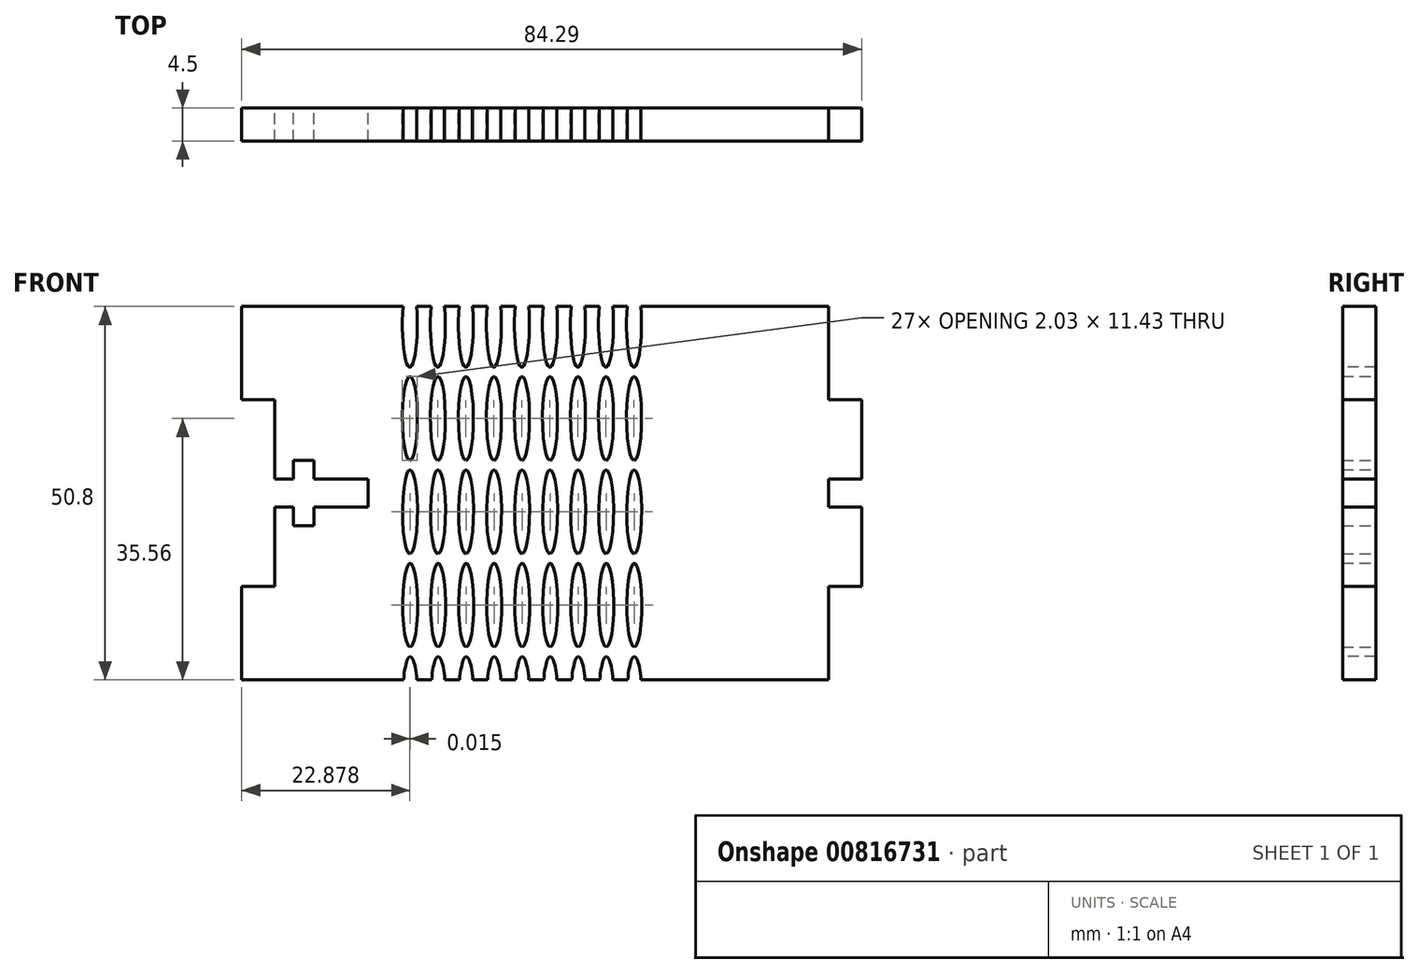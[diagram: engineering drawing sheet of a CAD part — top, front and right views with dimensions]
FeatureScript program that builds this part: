
annotation { "Feature Type Name" : "Feature", "Feature Type Description" : "" }
export const myFeature = defineFeature(function(context is Context, id is Id, definition is map)
    precondition{}
    {
        {
            var Q0;
            Q0=qCreatedBy(makeId("Front.planeOp"),FACE);
            var sketch = newSketch(context, id + "F0", { "sketchPlane" : qUnion([Q0])});
            skLineSegment(sketch, "E0.bottom", {"start": v(39.9, -25.4) * mm, "end": v(14.41, -25.4) * mm});
            skLineSegment(sketch, "E0.top", {"start": v(39.9, 25.4) * mm, "end": v(14.35, 25.4) * mm});
            skLineSegment(sketch, "E0.left", {"start": v(39.9, -25.4) * mm, "end": v(39.9, -12.7) * mm});
            skLineSegment(sketch, "E0.right", {"start": v(-39.9, -25.4) * mm, "end": v(-39.9, -12.7) * mm});
            skPoint(sketch, "E0.middle", {"position": v(0, 0) * mm});
            skLineSegment(sketch, "E1.bottom", {"start": v(-35.4, -12.7) * mm, "end": v(-39.9, -12.7) * mm});
            skLineSegment(sketch, "E1.top", {"start": v(-35.4, 12.7) * mm, "end": v(-39.9, 12.7) * mm});
            skLineSegment(sketch, "E1.left", {"start": v(-35.4, -12.7) * mm, "end": v(-35.4, -1.9) * mm});
            skPoint(sketch, "E1.middle", {"position": v(-39.9, 0) * mm});
            skLineSegment(sketch, "E2.bottom", {"start": v(-35.4, 1.9) * mm, "end": v(-32.86, 1.9) * mm});
            skLineSegment(sketch, "E2.top", {"start": v(-35.4, -1.9) * mm, "end": v(-32.86, -1.9) * mm});
            skLineSegment(sketch, "E2.right", {"start": v(-22.7, 1.9) * mm, "end": v(-22.7, -1.9) * mm});
            skPoint(sketch, "E2.middle", {"position": v(-29.05, 0) * mm});
            skPoint(sketch, "E2.middle.positionSnap0", {"position": v(-35.4, 0) * mm});
            skPoint(sketch, "E2.centerSnap0", {"position": v(-35.4, 0) * mm});
            skLineSegment(sketch, "E3.bottom", {"start": v(-30.07, -4.45) * mm, "end": v(-32.86, -4.45) * mm});
            skLineSegment(sketch, "E3.top", {"start": v(-30.07, 4.45) * mm, "end": v(-32.86, 4.45) * mm});
            skLineSegment(sketch, "E3.left", {"start": v(-30.07, -4.45) * mm, "end": v(-30.07, -1.9) * mm});
            skLineSegment(sketch, "E3.right", {"start": v(-32.86, -4.45) * mm, "end": v(-32.86, -1.9) * mm});
            skPoint(sketch, "E3.middle", {"position": v(-31.46, 0) * mm});
            skPoint(sketch, "E1.right.end.orphan", {"position": v(-44.4, 12.7) * mm});
            skPoint(sketch, "E4.orphan", {"position": v(-44.4, -12.7) * mm});
            skLineSegment(sketch, "E5.trimOffspring", {"start": v(-30.07, 1.9) * mm, "end": v(-22.7, 1.9) * mm});
            skLineSegment(sketch, "E6.trimOffspring", {"start": v(-30.07, -1.9) * mm, "end": v(-22.7, -1.9) * mm});
            skLineSegment(sketch, "E7.trimOffspring", {"start": v(-32.86, 1.9) * mm, "end": v(-32.86, 4.45) * mm});
            skLineSegment(sketch, "E8.trimOffspring", {"start": v(-30.07, 1.9) * mm, "end": v(-30.07, 4.45) * mm});
            skLineSegment(sketch, "E9.trimOffspring", {"start": v(-35.4, 1.9) * mm, "end": v(-35.4, 12.7) * mm});
            skLineSegment(sketch, "E10.trimOffspring", {"start": v(-39.9, 12.7) * mm, "end": v(-39.9, 25.4) * mm});
            skLineSegment(sketch, "E11.trimOffspring", {"start": v(39.9, 12.7) * mm, "end": v(39.9, 25.4) * mm});
            skLineSegment(sketch, "E12.bottom", {"start": v(39.9, 12.7) * mm, "end": v(44.4, 12.7) * mm});
            skLineSegment(sketch, "E12.top", {"start": v(39.69, -12.7) * mm, "end": v(44.4, -12.7) * mm});
            skLineSegment(sketch, "E12.right", {"start": v(44.4, 12.7) * mm, "end": v(44.4, 1.9) * mm});
            skPoint(sketch, "E13.MirrorCS.start.orphan", {"position": v(35.4, 12.7) * mm});
            skPoint(sketch, "E14.MirrorCS.start.orphan", {"position": v(35.4, -12.7) * mm});
            skLineSegment(sketch, "E15.bottom", {"start": v(44.4, -1.9) * mm, "end": v(39.9, -1.9) * mm});
            skLineSegment(sketch, "E15.top", {"start": v(44.4, 1.9) * mm, "end": v(39.9, 1.9) * mm});
            skLineSegment(sketch, "E15.right", {"start": v(39.9, -1.9) * mm, "end": v(39.9, 1.9) * mm});
            skPoint(sketch, "E15.middle", {"position": v(42.14, 0) * mm});
            skLineSegment(sketch, "E16.trimOffspring", {"start": v(44.4, -1.9) * mm, "end": v(44.4, -12.7) * mm});
            skEllipticalArc(sketch, "E17", {});
            skEllipse(sketch, "E18.0.1.0", {"center": v(-17.02, 10.16) * mm, "majorRadius": 5.72 * mm, "minorRadius": 1.02 * mm, "majorAxis": v(0, -1)});
            skEllipse(sketch, "E18.0.2.0", {"center": v(-17, -2.54) * mm, "majorRadius": 5.72 * mm, "minorRadius": 1.02 * mm, "majorAxis": v(0, -1)});
            skEllipse(sketch, "E18.0.3.0", {"center": v(-17, -15.24) * mm, "majorRadius": 5.72 * mm, "minorRadius": 1.02 * mm, "majorAxis": v(0, -1)});
            skEllipticalArc(sketch, "E18.0.4.0", {});
            skEllipticalArc(sketch, "E18.1.0.0", {});
            skEllipse(sketch, "E18.1.1.0", {"center": v(-13.21, 10.16) * mm, "majorRadius": 5.72 * mm, "minorRadius": 1.02 * mm, "majorAxis": v(0, -1)});
            skEllipse(sketch, "E18.1.2.0", {"center": v(-13.2, -2.54) * mm, "majorRadius": 5.72 * mm, "minorRadius": 1.02 * mm, "majorAxis": v(0, -1)});
            skEllipse(sketch, "E18.1.3.0", {"center": v(-13.18, -15.24) * mm, "majorRadius": 5.72 * mm, "minorRadius": 1.02 * mm, "majorAxis": v(0, -1)});
            skEllipticalArc(sketch, "E18.1.4.0", {});
            skEllipticalArc(sketch, "E18.2.0.0", {});
            skEllipse(sketch, "E18.2.1.0", {"center": v(-9.4, 10.16) * mm, "majorRadius": 5.72 * mm, "minorRadius": 1.02 * mm, "majorAxis": v(0, -1)});
            skEllipse(sketch, "E18.2.2.0", {"center": v(-9.39, -2.54) * mm, "majorRadius": 5.72 * mm, "minorRadius": 1.02 * mm, "majorAxis": v(0, -1)});
            skEllipse(sketch, "E18.2.3.0", {"center": v(-9.37, -15.24) * mm, "majorRadius": 5.72 * mm, "minorRadius": 1.02 * mm, "majorAxis": v(0, -1)});
            skEllipticalArc(sketch, "E18.2.4.0", {});
            skEllipticalArc(sketch, "E18.3.0.0", {});
            skEllipse(sketch, "E18.3.1.0", {"center": v(-5.6, 10.16) * mm, "majorRadius": 5.72 * mm, "minorRadius": 1.02 * mm, "majorAxis": v(0, -1)});
            skEllipse(sketch, "E18.3.2.0", {"center": v(-5.58, -2.54) * mm, "majorRadius": 5.72 * mm, "minorRadius": 1.02 * mm, "majorAxis": v(0, -1)});
            skEllipse(sketch, "E18.3.3.0", {"center": v(-5.56, -15.24) * mm, "majorRadius": 5.72 * mm, "minorRadius": 1.02 * mm, "majorAxis": v(0, -1)});
            skEllipticalArc(sketch, "E18.3.4.0", {});
            skEllipticalArc(sketch, "E18.4.0.0", {});
            skEllipse(sketch, "E18.4.1.0", {"center": v(-1.78, 10.16) * mm, "majorRadius": 5.72 * mm, "minorRadius": 1.02 * mm, "majorAxis": v(0, -1)});
            skEllipse(sketch, "E18.4.2.0", {"center": v(-1.77, -2.54) * mm, "majorRadius": 5.72 * mm, "minorRadius": 1.02 * mm, "majorAxis": v(0, -1)});
            skEllipse(sketch, "E18.4.3.0", {"center": v(-1.75, -15.24) * mm, "majorRadius": 5.72 * mm, "minorRadius": 1.02 * mm, "majorAxis": v(0, -1)});
            skEllipticalArc(sketch, "E18.4.4.0", {});
            skEllipticalArc(sketch, "E18.5.0.0", {});
            skEllipse(sketch, "E18.5.1.0", {"center": v(2.03, 10.16) * mm, "majorRadius": 5.72 * mm, "minorRadius": 1.02 * mm, "majorAxis": v(0, -1)});
            skEllipse(sketch, "E18.5.2.0", {"center": v(2.04, -2.54) * mm, "majorRadius": 5.72 * mm, "minorRadius": 1.02 * mm, "majorAxis": v(0, -1)});
            skEllipse(sketch, "E18.5.3.0", {"center": v(2.06, -15.24) * mm, "majorRadius": 5.72 * mm, "minorRadius": 1.02 * mm, "majorAxis": v(0, -1)});
            skEllipticalArc(sketch, "E18.5.4.0", {});
            skEllipticalArc(sketch, "E18.6.0.0", {});
            skEllipse(sketch, "E18.6.1.0", {"center": v(5.84, 10.16) * mm, "majorRadius": 5.72 * mm, "minorRadius": 1.02 * mm, "majorAxis": v(0, -1)});
            skEllipse(sketch, "E18.6.2.0", {"center": v(5.85, -2.54) * mm, "majorRadius": 5.72 * mm, "minorRadius": 1.02 * mm, "majorAxis": v(0, -1)});
            skEllipse(sketch, "E18.6.3.0", {"center": v(5.87, -15.24) * mm, "majorRadius": 5.72 * mm, "minorRadius": 1.02 * mm, "majorAxis": v(0, -1)});
            skEllipticalArc(sketch, "E18.6.4.0", {});
            skEllipticalArc(sketch, "E18.7.0.0", {});
            skEllipse(sketch, "E18.7.1.0", {"center": v(9.65, 10.16) * mm, "majorRadius": 5.72 * mm, "minorRadius": 1.02 * mm, "majorAxis": v(0, -1)});
            skEllipse(sketch, "E18.7.2.0", {"center": v(9.66, -2.54) * mm, "majorRadius": 5.72 * mm, "minorRadius": 1.02 * mm, "majorAxis": v(0, -1)});
            skEllipse(sketch, "E18.7.3.0", {"center": v(9.68, -15.24) * mm, "majorRadius": 5.72 * mm, "minorRadius": 1.02 * mm, "majorAxis": v(0, -1)});
            skEllipticalArc(sketch, "E18.7.4.0", {});
            skEllipticalArc(sketch, "E18.8.0.0", {});
            skEllipse(sketch, "E18.8.1.0", {"center": v(13.46, 10.16) * mm, "majorRadius": 5.72 * mm, "minorRadius": 1.02 * mm, "majorAxis": v(0, -1)});
            skEllipse(sketch, "E18.8.2.0", {"center": v(13.47, -2.54) * mm, "majorRadius": 5.72 * mm, "minorRadius": 1.02 * mm, "majorAxis": v(0, -1)});
            skEllipse(sketch, "E18.8.3.0", {"center": v(13.49, -15.24) * mm, "majorRadius": 5.72 * mm, "minorRadius": 1.02 * mm, "majorAxis": v(0, -1)});
            skEllipticalArc(sketch, "E18.8.4.0", {});
            skLineSegment(sketch, "E18.direction1", {"start": v(-17.04, 22.86) * mm, "end": v(-13.23, 22.86) * mm, "construction": true});
            skLineSegment(sketch, "E18.direction2", {"start": v(-17.04, 22.86) * mm, "end": v(-17.02, 10.16) * mm, "construction": true});
            skLineSegment(sketch, "E19.trimOffspring", {"start": v(-17.89, -25.4) * mm, "end": v(-39.9, -25.4) * mm});
            skLineSegment(sketch, "E20.trimOffspring", {"start": v(-14.08, -25.4) * mm, "end": v(-16.07, -25.4) * mm});
            skLineSegment(sketch, "E21.trimOffspring", {"start": v(-10.27, -25.4) * mm, "end": v(-12.26, -25.4) * mm});
            skLineSegment(sketch, "E22.trimOffspring", {"start": v(-6.46, -25.4) * mm, "end": v(-8.45, -25.4) * mm});
            skLineSegment(sketch, "E23.trimOffspring", {"start": v(-2.65, -25.4) * mm, "end": v(-4.64, -25.4) * mm});
            skLineSegment(sketch, "E24.trimOffspring", {"start": v(1.16, -25.4) * mm, "end": v(-0.83, -25.4) * mm});
            skLineSegment(sketch, "E25.trimOffspring", {"start": v(4.97, -25.4) * mm, "end": v(2.98, -25.4) * mm});
            skLineSegment(sketch, "E26.trimOffspring", {"start": v(8.78, -25.4) * mm, "end": v(6.8, -25.4) * mm});
            skLineSegment(sketch, "E27.trimOffspring", {"start": v(12.6, -25.4) * mm, "end": v(10.6, -25.4) * mm});
            skLineSegment(sketch, "E28.trimOffspring", {"start": v(12.53, 25.4) * mm, "end": v(10.54, 25.4) * mm});
            skLineSegment(sketch, "E29.trimOffspring", {"start": v(8.72, 25.4) * mm, "end": v(6.73, 25.4) * mm});
            skLineSegment(sketch, "E30.trimOffspring", {"start": v(4.91, 25.4) * mm, "end": v(2.92, 25.4) * mm});
            skLineSegment(sketch, "E31.trimOffspring", {"start": v(1.1, 25.4) * mm, "end": v(-0.89, 25.4) * mm});
            skLineSegment(sketch, "E32.trimOffspring", {"start": v(-2.7, 25.4) * mm, "end": v(-4.7, 25.4) * mm});
            skLineSegment(sketch, "E33.trimOffspring", {"start": v(-6.52, 25.4) * mm, "end": v(-8.5, 25.4) * mm});
            skLineSegment(sketch, "E34.trimOffspring", {"start": v(-10.33, 25.4) * mm, "end": v(-12.32, 25.4) * mm});
            skLineSegment(sketch, "E35.trimOffspring", {"start": v(-14.14, 25.4) * mm, "end": v(-16.13, 25.4) * mm});
            skLineSegment(sketch, "E36.trimOffspring", {"start": v(-17.95, 25.4) * mm, "end": v(-39.9, 25.4) * mm});
            const initialGuessF0  = {"E17": [-0.017037050000000005, 0.02286, 0, -1, 0.005715, 0.001016, 4.251834988703368, 2.031350318476219], "E18.0.4.0": [-0.016977518790876812, -0.027939965118444137, 0, -1, 0.005715, 0.001016, 2.0313435050632878, 4.251841802116299], "E18.1.0.0": [-0.013227050000000004, 0.02286, 0, -1, 0.005715, 0.001016, 4.251834988703367, 2.0313503184762185], "E18.1.4.0": [-0.013167518790876803, -0.02793996511844413, 0, -1, 0.005715, 0.001016, 2.0313435050632855, 4.251841802116292], "E18.2.0.0": [-0.009417050000000005, 0.02286, 0, -1, 0.005715, 0.001016, 4.251834988703367, 2.0313503184762185], "E18.2.4.0": [-0.009357518790876804, -0.02793996511844413, 0, -1, 0.005715, 0.001016, 2.0313435050632846, 4.251841802116292], "E18.3.0.0": [-0.005607050000000006, 0.02286, 0, -1, 0.005715, 0.001016, 4.251834988703367, 2.0313503184762176], "E18.3.4.0": [-0.005547518790876804, -0.027939965118444127, 0, -1, 0.005715, 0.001016, 2.0313435050632838, 4.2518418021162905], "E18.4.0.0": [-0.001797050000000005, 0.02286, 0, -1, 0.005715, 0.001016, 4.251834988703365, 2.031350318476217], "E18.4.4.0": [-0.0017375187908768037, -0.027939965118444127, 0, -1, 0.005715, 0.001016, 2.0313435050632846, 4.251841802116291], "E18.5.0.0": [0.002012949999999996, 0.02286, 0, -1, 0.005715, 0.001016, 4.251834988703363, 2.031350318476216], "E18.5.4.0": [0.002072481209123199, -0.027939965118444127, 0, -1, 0.005715, 0.001016, 2.0313435050632824, 4.251841802116289], "E18.6.0.0": [0.005822949999999993, 0.02286, 0, -1, 0.005715, 0.001016, 4.251834988703363, 2.031350318476216], "E18.6.4.0": [0.005882481209123196, -0.027939965118444127, 0, -1, 0.005715, 0.001016, 2.0313435050632824, 4.251841802116287], "E18.7.0.0": [0.009632949999999994, 0.02286, 0, -1, 0.005715, 0.001016, 4.251834988703363, 2.031350318476216], "E18.7.4.0": [0.009692481209123194, -0.027939965118444123, 0, -1, 0.005715, 0.001016, 2.0313435050632824, 4.251841802116287], "E18.8.0.0": [0.013442949999999995, 0.02286, 0, -1, 0.005715, 0.001016, 4.251834988703363, 2.0313503184762185], "E18.8.4.0": [0.013502481209123195, -0.027939965118444123, 0, -1, 0.005715, 0.001016, 2.0313435050632878, 4.2518418021162905]};
            skSetInitialGuess(sketch, initialGuessF0);
            skSolve(sketch);
        }
        {
            var Q0;
            Q0 = qSketchRegion(id + "F0", true);
            extrude(context, id + "F1", {"entities" : qUnion([Q0]), "depth" : 4.5 * mm, "offsetDistance" : 25.4 * mm, "symmetric" : true});
        }
    });
